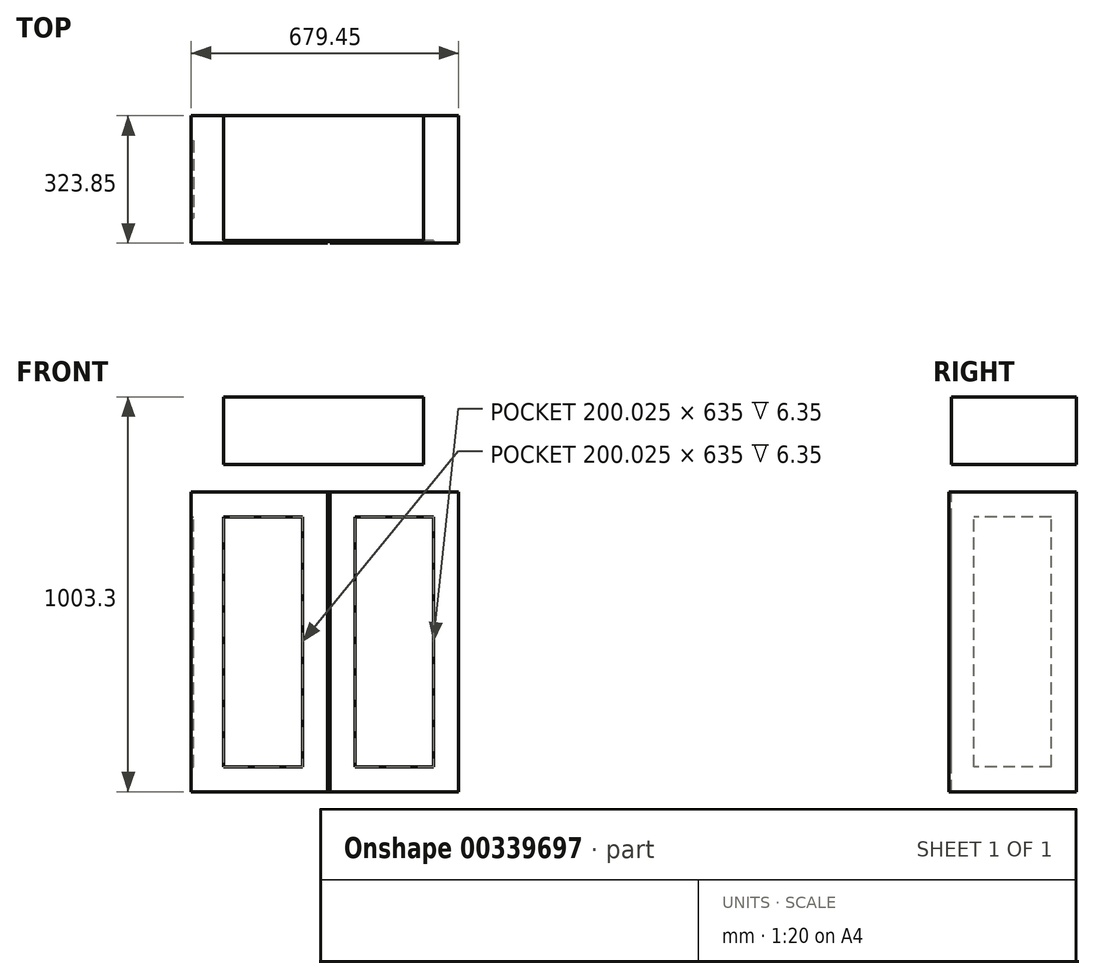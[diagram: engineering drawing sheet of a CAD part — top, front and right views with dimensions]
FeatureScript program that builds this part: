
annotation { "Feature Type Name" : "Feature", "Feature Type Description" : "" }
export const myFeature = defineFeature(function(context is Context, id is Id, definition is map)
    precondition{}
    {
        {
            var Q0;
            Q0=qCreatedBy(makeId("Front.planeOp"),FACE);
            var sketch = newSketch(context, id + "F0", { "sketchPlane" : qUnion([Q0])});
            skLineSegment(sketch, "E0.bottom", {"start": v(0, 0) * mm, "end": v(327.03, 0) * mm});
            skLineSegment(sketch, "E0.top", {"start": v(0, 762) * mm, "end": v(327.03, 762) * mm});
            skLineSegment(sketch, "E0.left", {"start": v(0, 0) * mm, "end": v(0, 762) * mm});
            skLineSegment(sketch, "E0.right", {"start": v(327.03, 0) * mm, "end": v(327.03, 762) * mm});
            skLineSegment(sketch, "E1.top", {"start": v(0, 1066.8) * mm, "end": v(660.4, 1066.8) * mm});
            skLineSegment(sketch, "E2.bottom", {"start": v(660.4, 0) * mm, "end": v(333.38, 0) * mm});
            skLineSegment(sketch, "E2.top", {"start": v(660.4, 762) * mm, "end": v(333.38, 762) * mm});
            skLineSegment(sketch, "E2.left", {"start": v(660.4, 0) * mm, "end": v(660.4, 762) * mm});
            skLineSegment(sketch, "E2.right", {"start": v(333.38, 0) * mm, "end": v(333.38, 762) * mm});
            skLineSegment(sketch, "E3.0", {"start": v(63.5, 1003.3) * mm, "end": v(571.5, 1003.3) * mm});
            skLineSegment(sketch, "E3.1", {"start": v(63.5, 831.85) * mm, "end": v(63.5, 1003.3) * mm});
            skLineSegment(sketch, "E3.2", {"start": v(63.5, 831.85) * mm, "end": v(571.5, 831.85) * mm});
            skLineSegment(sketch, "E3.3", {"start": v(571.5, 831.85) * mm, "end": v(571.5, 1003.3) * mm});
            skLineSegment(sketch, "E4.0", {"start": v(596.9, 698.5) * mm, "end": v(396.88, 698.5) * mm});
            skLineSegment(sketch, "E4.1", {"start": v(596.9, 63.5) * mm, "end": v(596.9, 698.5) * mm});
            skLineSegment(sketch, "E4.2", {"start": v(596.9, 63.5) * mm, "end": v(396.88, 63.5) * mm});
            skLineSegment(sketch, "E4.3", {"start": v(396.88, 63.5) * mm, "end": v(396.88, 698.5) * mm});
            skLineSegment(sketch, "E5.0", {"start": v(63.5, 698.5) * mm, "end": v(263.53, 698.5) * mm});
            skLineSegment(sketch, "E5.1", {"start": v(63.5, 63.5) * mm, "end": v(63.5, 698.5) * mm});
            skLineSegment(sketch, "E5.2", {"start": v(63.5, 63.5) * mm, "end": v(263.53, 63.5) * mm});
            skLineSegment(sketch, "E5.3", {"start": v(263.53, 63.5) * mm, "end": v(263.53, 698.5) * mm});
            skLineSegment(sketch, "E6", {"start": v(327.03, 0) * mm, "end": v(333.38, 0) * mm});
            skLineSegment(sketch, "E7", {"start": v(333.38, 762) * mm, "end": v(327.03, 762) * mm});
            skLineSegment(sketch, "E8", {"start": v(330.2, 762) * mm, "end": v(330.2, 796.5) * mm});
            skSolve(sketch);
        }
        {
            var Q0;
            Q0=makeQuery(id+"F0.imprint","IMPRINT",FACE,{"disambiguationData":[TD([[makeQuery(id+"F0.imprint","IMPRINT",EDGE,{"derivedFrom":sQuery(id+"F0.wireOp",EDGE,"E1.bottom")}),1.0]])]});
            var Q1;
            Q1=makeQuery(id+"F0.imprint","IMPRINT",FACE,{"disambiguationData":[TD([[makeQuery(id+"F0.imprint","IMPRINT",EDGE,{"derivedFrom":sQuery(id+"F0.wireOp",EDGE,"E3.0")}),-1.0]])]});
            var Q2;
            Q2=makeQuery(id+"F0.imprint","IMPRINT",FACE,{"disambiguationData":[TD([[makeQuery(id+"F0.imprint","IMPRINT",EDGE,{"derivedFrom":sQuery(id+"F0.wireOp",EDGE,"E0.bottom")}),1.0]])]});
            var Q3;
            Q3=makeQuery(id+"F0.imprint","IMPRINT",FACE,{"disambiguationData":[TD([[makeQuery(id+"F0.imprint","IMPRINT",EDGE,{"derivedFrom":sQuery(id+"F0.wireOp",EDGE,"E5.0")}),-1.0]])]});
            var Q4;
            Q4=makeQuery(id+"F0.imprint","IMPRINT",FACE,{"disambiguationData":[TD([[makeQuery(id+"F0.imprint","IMPRINT",EDGE,{"derivedFrom":sQuery(id+"F0.wireOp",EDGE,"E2.bottom")}),-1.0]])]});
            var Q5;
            Q5=makeQuery(id+"F0.imprint","IMPRINT",FACE,{"disambiguationData":[TD([[makeQuery(id+"F0.imprint","IMPRINT",EDGE,{"derivedFrom":sQuery(id+"F0.wireOp",EDGE,"E4.0")}),1.0]])]});
            var Q6;
            Q6=makeQuery(id+"F0.imprint","IMPRINT",FACE,{"disambiguationData":[TD([[makeQuery(id+"F0.imprint","IMPRINT",EDGE,{"derivedFrom":sQuery(id+"F0.wireOp",EDGE,"E0.top")}),1.0]])]});
            var Q7;
            Q7=makeQuery(id+"F0.imprint","IMPRINT",FACE,{"disambiguationData":[TD([[makeQuery(id+"F0.imprint","IMPRINT",EDGE,{"derivedFrom":sQuery(id+"F0.wireOp",EDGE,"E0.right")}),-1.0]])]});
            extrude(context, id + "F1", {"entities" : qUnion([Q0, Q1, Q2, Q3, Q4, Q5, Q6, Q7]), "oppositeDirection" : true, "depth" : 323.85 * mm, "offsetDistance" : 25.4 * mm});
        }
        {
            var Q0;
            Q0=makeQuery(id+"F0.imprint","IMPRINT",FACE,{"disambiguationData":[TD([[makeQuery(id+"F0.imprint","IMPRINT",EDGE,{"derivedFrom":sQuery(id+"F0.wireOp",EDGE,"E3.0")}),-1.0]])]});
            var Q1;
            Q1=makeQuery(id+"F0.imprint","IMPRINT",FACE,{"disambiguationData":[TD([[makeQuery(id+"F0.imprint","IMPRINT",EDGE,{"derivedFrom":sQuery(id+"F0.wireOp",EDGE,"E5.0")}),-1.0]])]});
            var Q2;
            Q2=makeQuery(id+"F0.imprint","IMPRINT",FACE,{"disambiguationData":[TD([[makeQuery(id+"F0.imprint","IMPRINT",EDGE,{"derivedFrom":sQuery(id+"F0.wireOp",EDGE,"E4.0")}),1.0]])]});
            var Q3;
            Q3=makeQuery(id+"F0.imprint","IMPRINT",FACE,{"disambiguationData":[TD([[makeQuery(id+"F0.imprint","IMPRINT",EDGE,{"derivedFrom":sQuery(id+"F0.wireOp",EDGE,"E0.top")}),1.0]])]});
            var Q4;
            Q4=makeQuery(id+"F0.imprint","IMPRINT",FACE,{"disambiguationData":[TD([[makeQuery(id+"F0.imprint","IMPRINT",EDGE,{"derivedFrom":sQuery(id+"F0.wireOp",EDGE,"E0.right")}),-1.0]])]});
            extrude(context, id + "F2", {"entities" : qUnion([Q0, Q1, Q2, Q3, Q4]), "operationType" : NewBodyOperationType.REMOVE, "oppositeDirection" : true, "depth" : 6.35 * mm, "offsetDistance" : 25.4 * mm});
        }
        {
            var Q0;
            Q0=makeQuery(id+"F1.opExtrude","SWEPT_FACE",FACE,{"disambiguationData":[OSD([sQuery(id+"F0.wireOp",EDGE,"E0.left")])]});
            var sketch = newSketch(context, id + "F3", { "sketchPlane" : qUnion([Q0])});
            skLineSegment(sketch, "E9.0", {"start": v(-260.35, 698.5) * mm, "end": v(-63.5, 698.5) * mm});
            skLineSegment(sketch, "E9.1", {"start": v(-260.35, 63.5) * mm, "end": v(-260.35, 698.5) * mm});
            skLineSegment(sketch, "E9.2", {"start": v(-260.35, 63.5) * mm, "end": v(-63.5, 63.5) * mm});
            skLineSegment(sketch, "E9.3", {"start": v(-63.5, 63.5) * mm, "end": v(-63.5, 698.5) * mm});
            skSolve(sketch);
        }
        {
            var Q0;
            Q0=makeQuery(id+"F3.imprint","IMPRINT",FACE,{"disambiguationData":[TD([[makeQuery(id+"F3.imprint","IMPRINT",EDGE,{"derivedFrom":sQuery(id+"F3.wireOp",EDGE,"E9.0")}),1.0]])]});
            extrude(context, id + "F4", {"entities" : qUnion([Q0]), "operationType" : NewBodyOperationType.ADD, "depth" : 19.05 * mm, "offsetDistance" : 25.4 * mm});
        }
        {
            var Q0;
            Q0=makeQuery(id+"F1.opExtrude","SWEPT_FACE",FACE,{"disambiguationData":[OSD([sQuery(id+"F0.wireOp",EDGE,"E0.left")])]});
            extrude(context, id + "F5", {"entities" : qUnion([Q0]), "operationType" : NewBodyOperationType.ADD, "depth" : 12.7 * mm, "offsetDistance" : 25.4 * mm});
        }
    });
